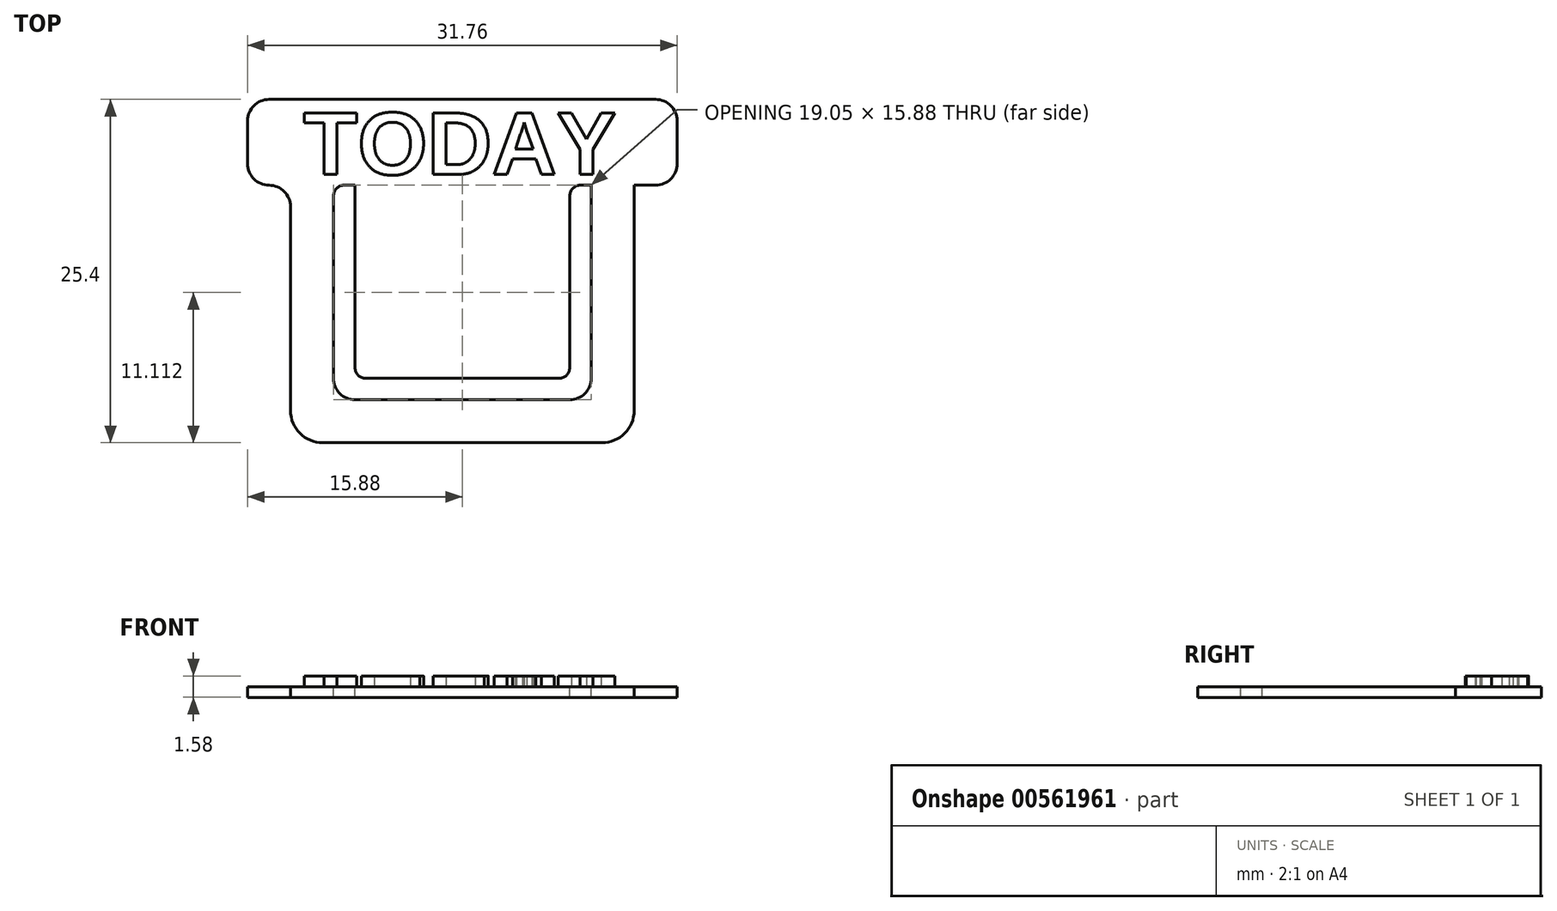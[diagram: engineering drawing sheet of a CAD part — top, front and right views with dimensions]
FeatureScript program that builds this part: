
annotation { "Feature Type Name" : "Feature", "Feature Type Description" : "" }
export const myFeature = defineFeature(function(context is Context, id is Id, definition is map)
    precondition{}
    {
        {
            var Q0;
            Q0=qCreatedBy(makeId("Front.planeOp"),FACE);
            var sketch = newSketch(context, id + "F0", { "sketchPlane" : qUnion([Q0])});
            skLineSegment(sketch, "E0.bottom", {"start": v(12.7, 9.53) * mm, "end": v(-12.7, 9.53) * mm});
            skLineSegment(sketch, "E0.top", {"start": v(12.7, -9.53) * mm, "end": v(-12.7, -9.53) * mm});
            skLineSegment(sketch, "E0.left", {"start": v(12.7, 9.53) * mm, "end": v(12.7, -9.53) * mm});
            skLineSegment(sketch, "E0.right", {"start": v(-12.7, 9.53) * mm, "end": v(-12.7, -9.53) * mm});
            skPoint(sketch, "E0.middle", {"position": v(0, 0) * mm});
            skSolve(sketch);
        }
        {
            var Q0;
            Q0=makeQuery(id+"F0.imprint","IMPRINT",FACE,{"disambiguationData":[TD([[makeQuery(id+"F0.imprint","IMPRINT",EDGE,{"derivedFrom":sQuery(id+"F0.wireOp",EDGE,"E0.bottom")}),1.0]])]});
            extrude(context, id + "F1", {"entities" : qUnion([Q0]), "depth" : 0.8 * mm, "offsetDistance" : 25.4 * mm});
        }
        {
            var Q0;
            Q0=makeQuery(id+"F1.opExtrude","SWEPT_EDGE",EDGE,{"disambiguationData":[OSD([sQuery(id+"F0.wireOp",EDGE,"E0.top"),sQuery(id+"F0.wireOp",EDGE,"E0.left")])]});
            var Q1;
            Q1=makeQuery(id+"F1.opExtrude","SWEPT_EDGE",EDGE,{"disambiguationData":[OSD([sQuery(id+"F0.wireOp",EDGE,"E0.top"),sQuery(id+"F0.wireOp",EDGE,"E0.right")])]});
            fillet(context, id + "F2", {"entities" : qUnion([Q0, Q1]), "radius" : 2.38 * mm, "tangentPropagation" : true, "allowEdgeOverflow" : false});
        }
        {
            var Q0;
            Q0=makeQuery(id+"F1.opExtrude","CAP_FACE",FACE,{"disambiguationData":[OSD([sQuery(id+"F0.wireOp",EDGE,"E0.bottom"),sQuery(id+"F0.wireOp",EDGE,"E0.top"),sQuery(id+"F0.wireOp",EDGE,"E0.left"),sQuery(id+"F0.wireOp",EDGE,"E0.right")])],"isStart":false});
            var sketch = newSketch(context, id + "F3", { "sketchPlane" : qUnion([Q0])});
            skLineSegment(sketch, "E1.bottom", {"start": v(9.52, 9.53) * mm, "end": v(-9.53, 9.53) * mm});
            skLineSegment(sketch, "E1.top", {"start": v(9.53, -6.35) * mm, "end": v(-9.53, -6.35) * mm});
            skLineSegment(sketch, "E1.left", {"start": v(9.52, 9.53) * mm, "end": v(9.53, -6.35) * mm});
            skLineSegment(sketch, "E1.right", {"start": v(-9.53, 9.53) * mm, "end": v(-9.52, -6.35) * mm});
            skPoint(sketch, "E1.middle", {"position": v(0, 0) * mm});
            skSolve(sketch);
        }
        {
            var Q0;
            Q0=makeQuery(id+"F3.imprint","IMPRINT",FACE,{"disambiguationData":[TD([[makeQuery(id+"F3.imprint","IMPRINT",EDGE,{"derivedFrom":sQuery(id+"F3.wireOp",EDGE,"E1.bottom")}),1.0]])]});
            extrude(context, id + "F4", {"entities" : qUnion([Q0]), "operationType" : NewBodyOperationType.REMOVE, "oppositeDirection" : true, "depth" : 4.93 * mm, "offsetDistance" : 25.4 * mm});
        }
        {
            var Q0;
            Q0=makeQuery(id+"F1.opExtrude","CAP_FACE",FACE,{"disambiguationData":[OSD([sQuery(id+"F0.wireOp",EDGE,"E0.bottom"),sQuery(id+"F0.wireOp",EDGE,"E0.top"),sQuery(id+"F0.wireOp",EDGE,"E0.left"),sQuery(id+"F0.wireOp",EDGE,"E0.right")])],"isStart":false});
            var sketch = newSketch(context, id + "F5", { "sketchPlane" : qUnion([Q0])});
            skLineSegment(sketch, "E2.bottom", {"start": v(-15.88, 9.53) * mm, "end": v(15.87, 9.53) * mm});
            skLineSegment(sketch, "E2.top", {"start": v(-15.88, 15.88) * mm, "end": v(15.87, 15.88) * mm});
            skLineSegment(sketch, "E2.left", {"start": v(-15.88, 9.53) * mm, "end": v(-15.88, 15.88) * mm});
            skLineSegment(sketch, "E2.right", {"start": v(15.87, 9.53) * mm, "end": v(15.87, 15.88) * mm});
            skSolve(sketch);
        }
        {
            var Q0;
            Q0=makeQuery(id+"F5.imprint","IMPRINT",FACE,{"disambiguationData":[TD([[makeQuery(id+"F5.imprint","IMPRINT",EDGE,{"derivedFrom":sQuery(id+"F5.wireOp",EDGE,"E2.top")}),-1.0]])]});
            extrude(context, id + "F6", {"entities" : qUnion([Q0]), "operationType" : NewBodyOperationType.ADD, "oppositeDirection" : true, "depth" : 0.8 * mm, "offsetDistance" : 25.4 * mm});
        }
        {
            var Q0;
            Q0=makeQuery(id+"F6.opExtrude","SWEPT_EDGE",EDGE,{"disambiguationData":[OSD([sQuery(id+"F5.wireOp",EDGE,"E2.top"),sQuery(id+"F5.wireOp",EDGE,"E2.left")])]});
            var Q1;
            Q1=makeQuery(id+"F6.opExtrude","SWEPT_EDGE",EDGE,{"disambiguationData":[OSD([sQuery(id+"F5.wireOp",EDGE,"E2.top"),sQuery(id+"F5.wireOp",EDGE,"E2.right")])]});
            var Q2;
            Q2=makeQuery(id+"F6.opExtrude","SWEPT_EDGE",EDGE,{"disambiguationData":[OSD([sQuery(id+"F5.wireOp",EDGE,"E2.bottom"),sQuery(id+"F5.wireOp",EDGE,"E2.right")])]});
            var Q3;
            Q3=makeQuery(id+"F1.opExtrude","SWEPT_EDGE",EDGE,{"disambiguationData":[OSD([sQuery(id+"F0.wireOp",EDGE,"E0.bottom"),sQuery(id+"F0.wireOp",EDGE,"E0.left")])]});
            var Q4;
            Q4=makeQuery(id+"F6.opExtrude","SWEPT_EDGE",EDGE,{"disambiguationData":[OSD([sQuery(id+"F5.wireOp",EDGE,"E2.bottom"),sQuery(id+"F5.wireOp",EDGE,"E2.left")])]});
            var Q5;
            Q5=makeQuery(id+"F1.opExtrude","SWEPT_EDGE",EDGE,{"disambiguationData":[OSD([sQuery(id+"F0.wireOp",EDGE,"E0.bottom"),sQuery(id+"F0.wireOp",EDGE,"E0.right")])]});
            fillet(context, id + "F7", {"entities" : qUnion([Q0, Q1, Q2, Q3, Q4, Q5]), "radius" : 1.59 * mm, "tangentPropagation" : true, "allowEdgeOverflow" : false});
        }
        {
            var Q0;
            Q0=makeQuery(id+"F4.boolean.opBoolean","COPY",EDGE,{"derivedFrom":makeQuery(id+"F4.opExtrude","SWEPT_EDGE",EDGE,{"disambiguationData":[OSD([sQuery(id+"F3.wireOp",EDGE,"E1.top"),sQuery(id+"F3.wireOp",EDGE,"E1.right")])]})});
            var Q1;
            Q1=makeQuery(id+"F4.boolean.opBoolean","COPY",EDGE,{"derivedFrom":makeQuery(id+"F4.opExtrude","SWEPT_EDGE",EDGE,{"disambiguationData":[OSD([sQuery(id+"F3.wireOp",EDGE,"E1.top"),sQuery(id+"F3.wireOp",EDGE,"E1.left")])]})});
            fillet(context, id + "F8", {"entities" : qUnion([Q0, Q1]), "radius" : 1.59 * mm, "tangentPropagation" : true, "allowEdgeOverflow" : false});
        }
        {
            var Q0;
            Q0=makeQuery(id+"F6.boolean.opBoolean","MERGE",FACE,{"derivedFrom":[makeQuery(id+"F1.opExtrude","CAP_FACE",FACE,{"disambiguationData":[OSD([sQuery(id+"F0.wireOp",EDGE,"E0.bottom"),sQuery(id+"F0.wireOp",EDGE,"E0.top"),sQuery(id+"F0.wireOp",EDGE,"E0.left"),sQuery(id+"F0.wireOp",EDGE,"E0.right")])],"isStart":false}),makeQuery(id+"F6.opExtrude","CAP_FACE",FACE,{"disambiguationData":[OSD([sQuery(id+"F5.wireOp",EDGE,"E2.bottom"),sQuery(id+"F5.wireOp",EDGE,"E2.top"),sQuery(id+"F5.wireOp",EDGE,"E2.left"),sQuery(id+"F5.wireOp",EDGE,"E2.right")])],"isStart":true})]});
            var sketch = newSketch(context, id + "F9", { "sketchPlane" : qUnion([Q0])});
            skLineSegment(sketch, "E3.bottom", {"start": v(-7.94, 9.53) * mm, "end": v(7.94, 9.53) * mm});
            skLineSegment(sketch, "E3.top", {"start": v(-7.94, -4.76) * mm, "end": v(7.94, -4.76) * mm});
            skLineSegment(sketch, "E3.left", {"start": v(-7.94, 9.53) * mm, "end": v(-7.94, -4.76) * mm});
            skLineSegment(sketch, "E3.right", {"start": v(7.94, 9.53) * mm, "end": v(7.94, -4.76) * mm});
            skSolve(sketch);
        }
        {
            var Q0;
            Q0=makeQuery(id+"F9.imprint","IMPRINT",FACE,{"disambiguationData":[TD([[makeQuery(id+"F9.imprint","IMPRINT",EDGE,{"derivedFrom":sQuery(id+"F9.wireOp",EDGE,"E3.bottom")}),1.0]])]});
            extrude(context, id + "F10", {"entities" : qUnion([Q0]), "operationType" : NewBodyOperationType.ADD, "oppositeDirection" : true, "depth" : 0.8 * mm, "offsetDistance" : 25.4 * mm});
        }
        {
            var Q0;
            Q0=makeQuery(id+"F10.boolean.opBoolean","MERGE",FACE,{"derivedFrom":[makeQuery(id+"F6.boolean.opBoolean","MERGE",FACE,{"derivedFrom":[makeQuery(id+"F1.opExtrude","CAP_FACE",FACE,{"disambiguationData":[OSD([sQuery(id+"F0.wireOp",EDGE,"E0.bottom"),sQuery(id+"F0.wireOp",EDGE,"E0.top"),sQuery(id+"F0.wireOp",EDGE,"E0.left"),sQuery(id+"F0.wireOp",EDGE,"E0.right")])],"isStart":false}),makeQuery(id+"F6.opExtrude","CAP_FACE",FACE,{"disambiguationData":[OSD([sQuery(id+"F5.wireOp",EDGE,"E2.bottom"),sQuery(id+"F5.wireOp",EDGE,"E2.top"),sQuery(id+"F5.wireOp",EDGE,"E2.left"),sQuery(id+"F5.wireOp",EDGE,"E2.right")])],"isStart":true})]}),makeQuery(id+"F10.opExtrude","CAP_FACE",FACE,{"disambiguationData":[OSD([sQuery(id+"F9.wireOp",EDGE,"E3.bottom"),sQuery(id+"F9.wireOp",EDGE,"E3.top"),sQuery(id+"F9.wireOp",EDGE,"E3.left"),sQuery(id+"F9.wireOp",EDGE,"E3.right")])],"isStart":true})]});
            var sketch = newSketch(context, id + "F11", { "sketchPlane" : qUnion([Q0])});
            skText(sketch, "E4", { "text": "TODAY", "fontName": "Arimo-Bold.ttf"});
            const initialGuessF11  = {"E4": [-0.01177, 0.01032, 1, 0, 0.00476]};
            skSetInitialGuess(sketch, initialGuessF11);
            skSolve(sketch);
        }
        {
            var Q0;
            Q0=makeQuery(id+"F11.imprint","IMPRINT",FACE,{"disambiguationData":[TD([[makeQuery(id+"F11.imprint","IMPRINT",EDGE,{"derivedFrom":sQuery(id+"F11.wireOp",EDGE,"E4.sketch_text.stroke-0")}),-1.0]])]});
            var Q1;
            Q1=makeQuery(id+"F11.imprint","IMPRINT",FACE,{"disambiguationData":[TD([[makeQuery(id+"F11.imprint","IMPRINT",EDGE,{"derivedFrom":sQuery(id+"F11.wireOp",EDGE,"E4.sketch_text.stroke-8")}),-1.0]])]});
            var Q2;
            Q2=makeQuery(id+"F11.imprint","IMPRINT",FACE,{"disambiguationData":[TD([[makeQuery(id+"F11.imprint","IMPRINT",EDGE,{"derivedFrom":sQuery(id+"F11.wireOp",EDGE,"E4.sketch_text.stroke-25")}),-1.0]])]});
            var Q3;
            Q3=makeQuery(id+"F11.imprint","IMPRINT",FACE,{"disambiguationData":[TD([[makeQuery(id+"F11.imprint","IMPRINT",EDGE,{"derivedFrom":sQuery(id+"F11.wireOp",EDGE,"E4.sketch_text.stroke-40")}),-1.0]])]});
            var Q4;
            Q4=makeQuery(id+"F11.imprint","IMPRINT",FACE,{"disambiguationData":[TD([[makeQuery(id+"F11.imprint","IMPRINT",EDGE,{"derivedFrom":sQuery(id+"F11.wireOp",EDGE,"E4.sketch_text.stroke-55")}),-1.0]])]});
            extrude(context, id + "F12", {"entities" : qUnion([Q0, Q1, Q2, Q3, Q4]), "operationType" : NewBodyOperationType.ADD, "depth" : 0.8 * mm, "offsetDistance" : 25.4 * mm});
        }
        {
            var Q0;
            Q0=makeQuery(id+"F10.opExtrude","SWEPT_EDGE",EDGE,{"disambiguationData":[OSD([sQuery(id+"F5.wireOp",EDGE,"E2.bottom"),sQuery(id+"F9.wireOp",EDGE,"E3.bottom"),sQuery(id+"F9.wireOp",EDGE,"E3.left")])]});
            var Q1;
            Q1=makeQuery(id+"F4.boolean.opBoolean","COPY",EDGE,{"derivedFrom":makeQuery(id+"F4.opExtrude","SWEPT_EDGE",EDGE,{"disambiguationData":[OSD([sQuery(id+"F0.wireOp",EDGE,"E0.bottom"),sQuery(id+"F3.wireOp",EDGE,"E1.bottom"),sQuery(id+"F3.wireOp",EDGE,"E1.right")])]})});
            var Q2;
            Q2=makeQuery(id+"F10.opExtrude","SWEPT_EDGE",EDGE,{"disambiguationData":[OSD([sQuery(id+"F5.wireOp",EDGE,"E2.bottom"),sQuery(id+"F9.wireOp",EDGE,"E3.bottom"),sQuery(id+"F9.wireOp",EDGE,"E3.right")])]});
            var Q3;
            Q3=makeQuery(id+"F4.boolean.opBoolean","COPY",EDGE,{"derivedFrom":makeQuery(id+"F4.opExtrude","SWEPT_EDGE",EDGE,{"disambiguationData":[OSD([sQuery(id+"F0.wireOp",EDGE,"E0.bottom"),sQuery(id+"F3.wireOp",EDGE,"E1.bottom"),sQuery(id+"F3.wireOp",EDGE,"E1.left")])]})});
            fillet(context, id + "F13", {"entities" : qUnion([Q0, Q1, Q2, Q3]), "radius" : 0.8 * mm, "tangentPropagation" : true, "allowEdgeOverflow" : false});
        }
        {
            var Q0;
            Q0=makeQuery(id+"F10.opExtrude","SWEPT_EDGE",EDGE,{"disambiguationData":[OSD([sQuery(id+"F9.wireOp",EDGE,"E3.top"),sQuery(id+"F9.wireOp",EDGE,"E3.left")])]});
            var Q1;
            Q1=makeQuery(id+"F10.opExtrude","SWEPT_EDGE",EDGE,{"disambiguationData":[OSD([sQuery(id+"F9.wireOp",EDGE,"E3.top"),sQuery(id+"F9.wireOp",EDGE,"E3.right")])]});
            fillet(context, id + "F14", {"entities" : qUnion([Q0, Q1]), "radius" : 0.8 * mm, "tangentPropagation" : true, "allowEdgeOverflow" : false});
        }
        {
            var Q0;
            Q0=makeQuery(id+"F1.opExtrude","SWEPT_BODY",BODY,{"disambiguationData":[OSD([sQuery(id+"F0.wireOp",EDGE,"E0.bottom"),sQuery(id+"F0.wireOp",EDGE,"E0.top"),sQuery(id+"F0.wireOp",EDGE,"E0.left"),sQuery(id+"F0.wireOp",EDGE,"E0.right")])]});
            var Q1;
            Q1=makeQuery(id+"F6.opExtrude","CAP_EDGE",EDGE,{"disambiguationData":[OSD([sQuery(id+"F5.wireOp",EDGE,"E2.top")])],"isStart":false});
            transform(context, id + "F15", {"entities" : qUnion([Q0]), "transformType" : TransformType.ROTATION, "transformAxis" : qUnion([Q1]), "angle" : 270 * degree, "makeCopy" : false});
        }
    });
